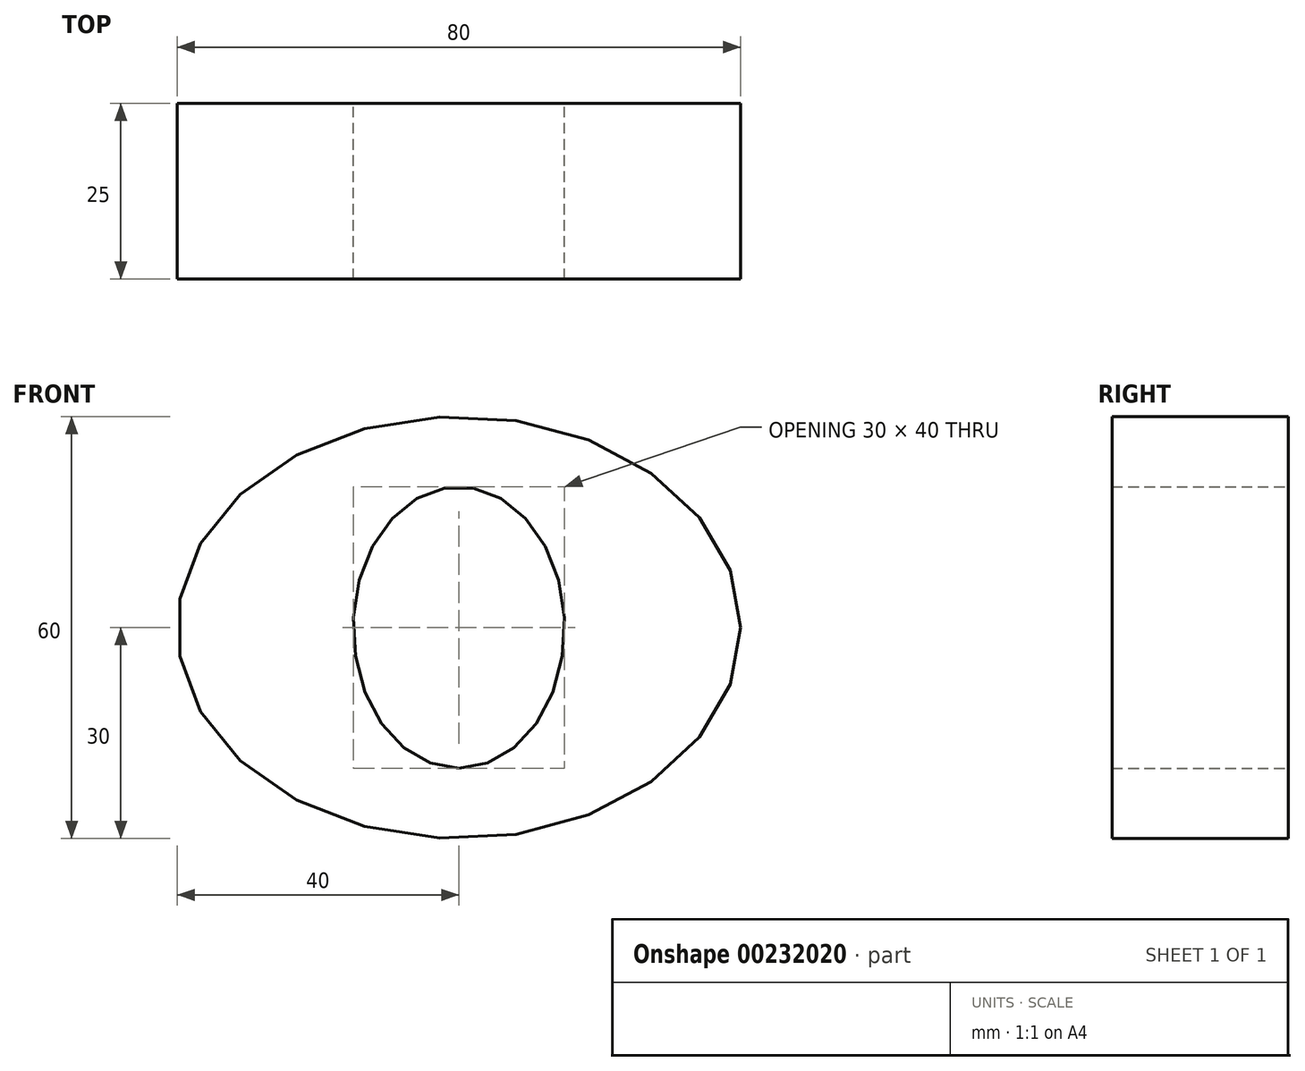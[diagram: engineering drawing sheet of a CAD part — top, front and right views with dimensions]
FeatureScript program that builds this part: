
annotation { "Feature Type Name" : "Feature", "Feature Type Description" : "" }
export const myFeature = defineFeature(function(context is Context, id is Id, definition is map)
    precondition{}
    {
        {
            var Q0;
            Q0=qCreatedBy(makeId("Front.planeOp"),FACE);
            var sketch = newSketch(context, id + "F0", { "sketchPlane" : qUnion([Q0])});
            skEllipse(sketch, "E0", {"center": v(0, 0) * mm, "majorRadius": 20 * mm, "minorRadius": 15 * mm, "majorAxis": v(0, -1)});
            skEllipse(sketch, "E1", {"center": v(0, 0) * mm, "majorRadius": 40 * mm, "minorRadius": 30 * mm, "majorAxis": v(1, 0)});
            skSolve(sketch);
        }
        {
            var Q0;
            Q0=makeQuery(id+"F0.imprint","IMPRINT",FACE,{"disambiguationData":[TD([[makeQuery(id+"F0.imprint","IMPRINT",EDGE,{"derivedFrom":sQuery(id+"F0.wireOp",EDGE,"E0")}),-1.0]])]});
            extrude(context, id + "F1", {"entities" : qUnion([Q0]), "depth" : 25 * mm});
        }
    });
